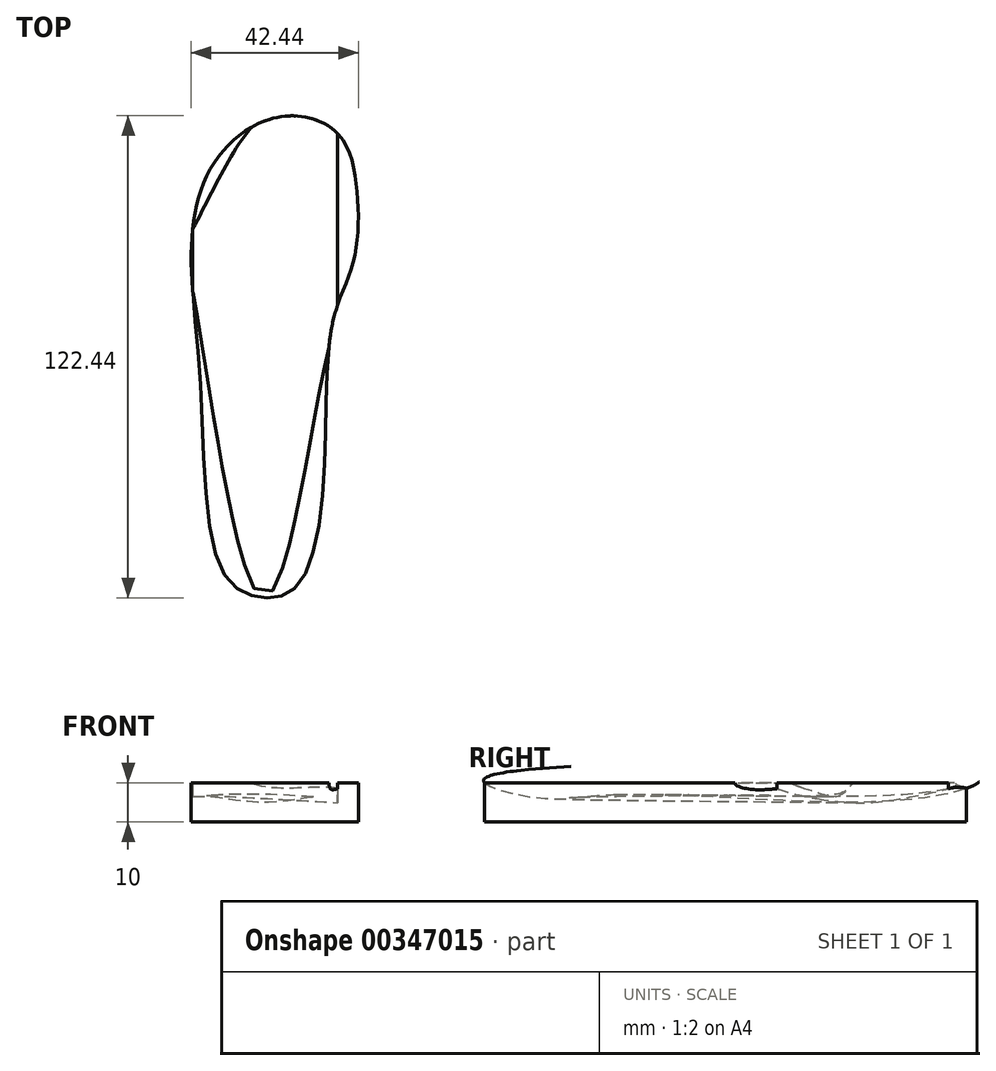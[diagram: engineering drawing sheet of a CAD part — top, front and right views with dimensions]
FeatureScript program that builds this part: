
annotation { "Feature Type Name" : "Feature", "Feature Type Description" : "" }
export const myFeature = defineFeature(function(context is Context, id is Id, definition is map)
    precondition{}
    {
        {
            var Q0;
            Q0=qCreatedBy(makeId("Top.planeOp"),FACE);
            var sketch = newSketch(context, id + "F0", { "sketchPlane" : qUnion([Q0])});
            skFitSpline(sketch, "E0", {"points": [v(19.34, 60.67) * mm, v(24, 46) * mm, v(23.11, 28.67) * mm, v(17.78, 12.9) * mm, v(15.78, -22.9) * mm, v(9.11, -53.56) * mm, v(0, -56.9) * mm, v(-10.22, -50.23) * mm, v(-15.78, -2.89) * mm, v(-18, 34.23) * mm, v(-10.9, 55.56) * mm, v(5.33, 65.34) * mm, v(19.34, 60.67) * mm]});
            skSolve(sketch);
        }
        {
            var Q0;
            Q0 = qSketchRegion(id + "F0", true);
            extrude(context, id + "F1", {"entities" : qUnion([Q0]), "depth" : 10 * mm});
        }
        {
            var Q0;
            Q0=qCreatedBy(makeId("Right.planeOp"),FACE);
            var sketch = newSketch(context, id + "F2", { "sketchPlane" : qUnion([Q0])});
            skLineSegment(sketch, "E1", {"start": v(65.22, 11.2) * mm, "end": v(-56.67, 11.2) * mm});
            skFitSpline(sketch, "E2", {"points": [v(65.22, 11.2) * mm, v(58.45, 7.33) * mm, v(25.56, 5.33) * mm, v(-24.35, 6.97) * mm, v(-45.39, 6.48) * mm, v(-56.67, 11.2) * mm, v(65.22, 11.2) * mm]});
            skSolve(sketch);
        }
        {
            var Q0;
            Q0=qCreatedBy(makeId("Right.planeOp"),FACE);
            cPlane(context, id + "F3", {"entities" : qUnion([Q0]), "cplaneType" : CPlaneType.OFFSET, "offset" : 19.05 * mm, "width" : 152.4 * mm, "height" : 152.4 * mm});
        }
        {
            var Q0;
            Q0=qCreatedBy(makeId("Right.planeOp"),FACE);
            cPlane(context, id + "F4", {"entities" : qUnion([Q0]), "cplaneType" : CPlaneType.OFFSET, "offset" : 17.78 * mm, "oppositeDirection" : true, "width" : 152.4 * mm, "height" : 152.4 * mm});
        }
        {
            var Q0;
            Q0=qCreatedBy(id+"F3.planeOp",FACE);
            var sketch = newSketch(context, id + "F5", { "sketchPlane" : qUnion([Q0])});
            skFitSpline(sketch, "E3", {"points": [v(15.45, 10.56) * mm, v(31.05, 5.42) * mm, v(51.7, 6.45) * mm, v(66.1, 10.38) * mm, v(66, 11.4) * mm, v(15.45, 10.56) * mm]});
            skSolve(sketch);
        }
        {
            var Q0;
            Q0=qCreatedBy(id+"F4.planeOp",FACE);
            var sketch = newSketch(context, id + "F6", { "sketchPlane" : qUnion([Q0])});
            skFitSpline(sketch, "E4", {"points": [v(19.9, 11.07) * mm, v(28.03, 7.41) * mm, v(33.56, 6.95) * mm, v(37.4, 10.74) * mm, v(37.43, 11.12) * mm, v(19.9, 11.07) * mm]});
            skSolve(sketch);
        }
        {
            var Q0;
            Q0=makeQuery(id+"F5.imprint","IMPRINT",FACE,{"disambiguationData":[TD([[makeQuery(id+"F5.imprint","IMPRINT",EDGE,{"derivedFrom":sQuery(id+"F5.wireOp",EDGE,"E3")}),1.0]])]});
            var Q1;
            Q1 = qSketchRegion(id + "F2", true);
            var Q2;
            Q2 = qSketchRegion(id + "F6", true);
            loft(context, id + "F7", {"operationType" : NewBodyOperationType.REMOVE, "sheetProfilesArray" : [{ "sheetProfileEntities" : qUnion([Q0]) }, { "sheetProfileEntities" : qUnion([Q1]) }, { "sheetProfileEntities" : qUnion([Q2]) }]});
        }
    });
